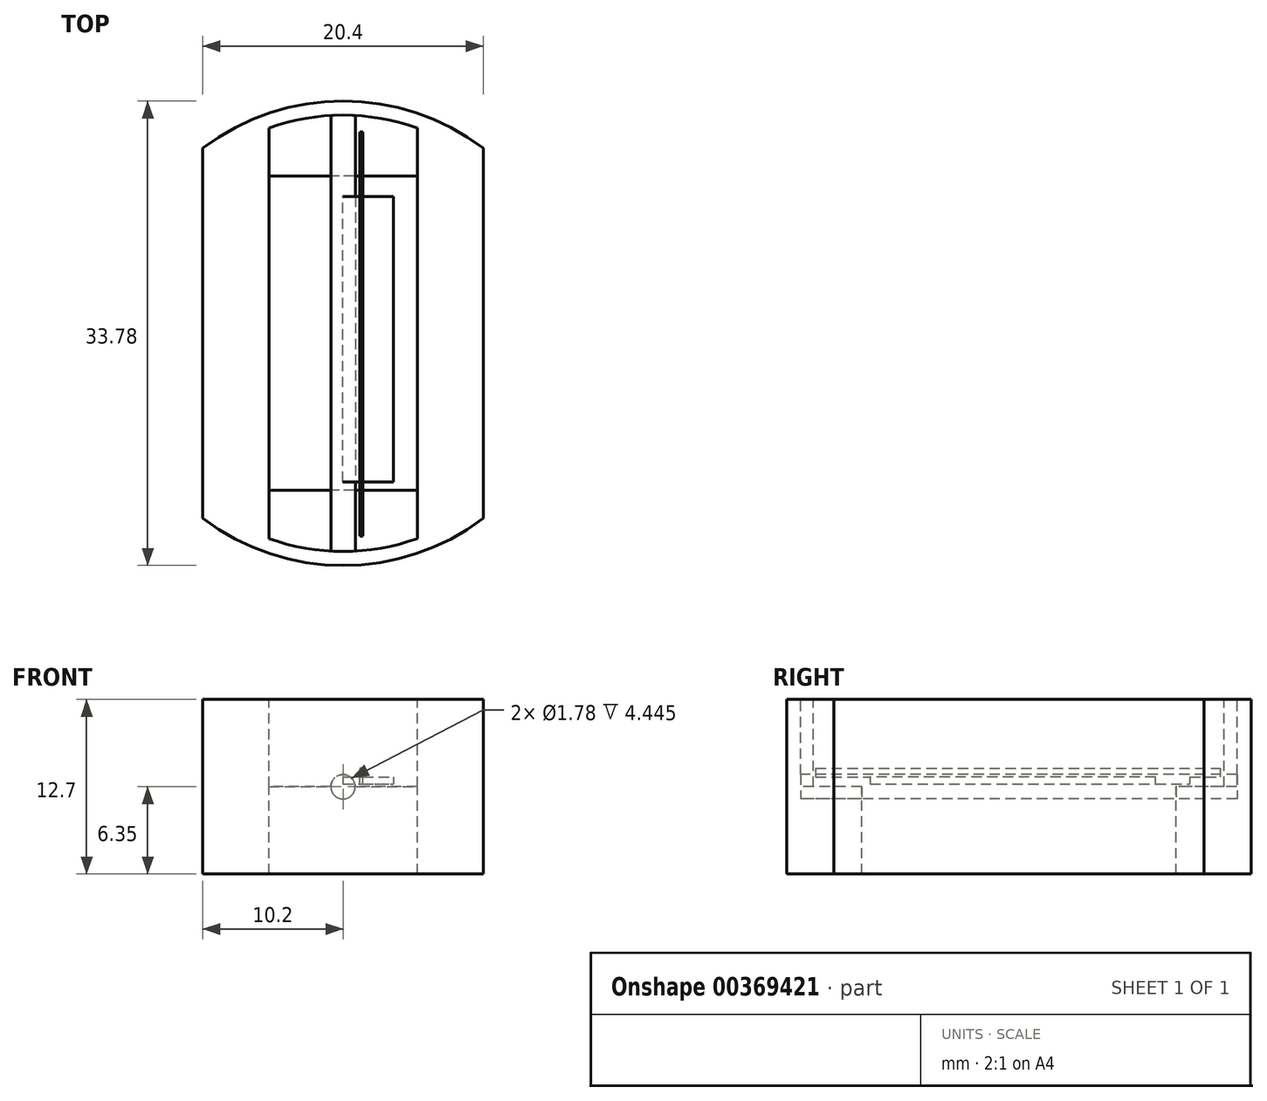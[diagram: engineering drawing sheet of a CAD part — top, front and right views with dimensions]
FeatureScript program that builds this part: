
annotation { "Feature Type Name" : "Feature", "Feature Type Description" : "" }
export const myFeature = defineFeature(function(context is Context, id is Id, definition is map)
    precondition{}
    {
        {
            var Q0;
            Q0=qCreatedBy(makeId("Top.planeOp"),FACE);
            var sketch = newSketch(context, id + "F0", { "sketchPlane" : qUnion([Q0])});
            skCircle(sketch, "E0", {"center": v(0, 0) * mm, "radius": 16.9 * mm});
            skSolve(sketch);
        }
        {
            var Q0;
            Q0 = qSketchRegion(id + "F0", true);
            var Q1;
            Q1 = qSketchRegion(id + "FndjnpffMJqqSbx_1", true);
            extrude(context, id + "F1", {"entities" : qUnion([Q0, Q1]), "depth" : 12.7 * mm});
        }
        {
            var Q0;
            Q0=qCreatedBy(makeId("Top.planeOp"),FACE);
            var sketch = newSketch(context, id + "F2", { "sketchPlane" : qUnion([Q0])});
            skLineSegment(sketch, "E1.bottom", {"start": v(-10.2, -16.71) * mm, "end": v(-23.15, -16.71) * mm});
            skLineSegment(sketch, "E1.top", {"start": v(-10.2, 16.78) * mm, "end": v(-23.15, 16.78) * mm});
            skLineSegment(sketch, "E1.left", {"start": v(-10.2, -16.71) * mm, "end": v(-10.2, 16.78) * mm});
            skLineSegment(sketch, "E1.right", {"start": v(-23.15, -16.71) * mm, "end": v(-23.15, 16.78) * mm});
            skSolve(sketch);
        }
        {
            var Q0;
            Q0=qCreatedBy(makeId("Top.planeOp"),FACE);
            var sketch = newSketch(context, id + "F3", { "sketchPlane" : qUnion([Q0])});
            skLineSegment(sketch, "E2.bottom", {"start": v(10.2, -16.64) * mm, "end": v(26.8, -16.64) * mm});
            skLineSegment(sketch, "E2.top", {"start": v(10.2, 17) * mm, "end": v(26.8, 17) * mm});
            skLineSegment(sketch, "E2.left", {"start": v(10.2, -16.64) * mm, "end": v(10.2, 17) * mm});
            skLineSegment(sketch, "E2.right", {"start": v(26.8, -16.64) * mm, "end": v(26.8, 17) * mm});
            skSolve(sketch);
        }
        {
            var Q0;
            Q0=makeQuery(id+"F2.imprint","IMPRINT",FACE,{"disambiguationData":[TD([[makeQuery(id+"F2.imprint","IMPRINT",EDGE,{"derivedFrom":sQuery(id+"F2.wireOp",EDGE,"E1.bottom")}),-1.0]])]});
            var Q1;
            Q1=makeQuery(id+"F3.imprint","IMPRINT",FACE,{"disambiguationData":[TD([[makeQuery(id+"F3.imprint","IMPRINT",EDGE,{"derivedFrom":sQuery(id+"F3.wireOp",EDGE,"E2.bottom")}),1.0]])]});
            extrude(context, id + "F4", {"entities" : qUnion([Q0, Q1]), "depth" : 12.7 * mm});
        }
        {
            var Q0;
            Q0=makeQuery(id+"F4.opExtrude","SWEPT_BODY",BODY,{"disambiguationData":[OSD([sQuery(id+"F2.wireOp",EDGE,"E1.bottom"),sQuery(id+"F2.wireOp",EDGE,"E1.top"),sQuery(id+"F2.wireOp",EDGE,"E1.left"),sQuery(id+"F2.wireOp",EDGE,"E1.right")])]});
            var Q1;
            Q1=makeQuery(id+"F4.opExtrude","SWEPT_BODY",BODY,{"disambiguationData":[OSD([sQuery(id+"F3.wireOp",EDGE,"E2.bottom"),sQuery(id+"F3.wireOp",EDGE,"E2.top"),sQuery(id+"F3.wireOp",EDGE,"E2.left"),sQuery(id+"F3.wireOp",EDGE,"E2.right")])]});
            var Q2;
            Q2=makeQuery(id+"F1.opExtrude","SWEPT_BODY",BODY,{"disambiguationData":[OSD([sQuery(id+"F0.wireOp",EDGE,"E0")])]});
            booleanBodies(context, id + "F5", {"operationType" : BooleanOperationType.SUBTRACTION, "tools" : qUnion([Q0, Q1]), "targets" : qUnion([Q2])});
        }
        {
            var Q0;
            Q0=qCreatedBy(makeId("Top.planeOp"),FACE);
            var sketch = newSketch(context, id + "F6", { "sketchPlane" : qUnion([Q0])});
            skLineSegment(sketch, "E3.bottom", {"start": v(5.4, -15.88) * mm, "end": v(-5.4, -15.88) * mm});
            skLineSegment(sketch, "E3.top", {"start": v(5.4, 15.88) * mm, "end": v(-5.4, 15.88) * mm});
            skLineSegment(sketch, "E3.left", {"start": v(5.4, -15.88) * mm, "end": v(5.4, 15.88) * mm});
            skLineSegment(sketch, "E3.right", {"start": v(-5.4, -15.88) * mm, "end": v(-5.4, 15.88) * mm});
            skPoint(sketch, "E3.middle", {"position": v(0, 0) * mm});
            skCircle(sketch, "E4", {"center": v(0, 0) * mm, "radius": 15.88 * mm});
            skSolve(sketch);
        }
        {
            var Q0;
            {var subQ0=sQuery(id+"F6.wireOp",EDGE,"E4");var subQ5=sQuery(id+"F6.wireOp",EDGE,"E3.left");var subQ7=makeQuery(id+"F6.imprint","INTERSECT",VERTEX,{"disambiguationData":[OD(0.0)],"derivedFrom":[subQ5,subQ0]});Q0=makeQuery(id+"F6.imprint","IMPRINT",FACE,{"disambiguationData":[TD([[makeQuery(id+"F6.imprint","IMPRINT",EDGE,{"disambiguationData":[TD([[subQ7,-1.0]])],"derivedFrom":subQ5}),1.0]])]});}
            extrude(context, id + "F7", {"entities" : qUnion([Q0]), "depth" : 6.35 * mm});
        }
        {
            var Q0;
            Q0=makeQuery(id+"F7.opExtrude","SWEPT_BODY",BODY,{"disambiguationData":[OSD([sQuery(id+"F6.wireOp",EDGE,"E3.left"),sQuery(id+"F6.wireOp",EDGE,"E3.right"),sQuery(id+"F6.wireOp",EDGE,"E4")])]});
            var Q1;
            Q1=makeQuery(id+"F1.opExtrude","SWEPT_BODY",BODY,{"disambiguationData":[OSD([sQuery(id+"F0.wireOp",EDGE,"E0")])]});
            booleanBodies(context, id + "F8", {"operationType" : BooleanOperationType.SUBTRACTION, "tools" : qUnion([Q0]), "targets" : qUnion([Q1])});
        }
        {
            var Q0;
            Q0=qCreatedBy(makeId("Top.planeOp"),FACE);
            var sketch = newSketch(context, id + "F9", { "sketchPlane" : qUnion([Q0])});
            skLineSegment(sketch, "E5.bottom", {"start": v(5.4, -11.43) * mm, "end": v(-5.4, -11.43) * mm});
            skLineSegment(sketch, "E5.top", {"start": v(5.4, 11.43) * mm, "end": v(-5.4, 11.43) * mm});
            skLineSegment(sketch, "E5.left", {"start": v(5.4, -11.43) * mm, "end": v(5.4, 11.43) * mm});
            skLineSegment(sketch, "E5.right", {"start": v(-5.4, -11.43) * mm, "end": v(-5.4, 11.43) * mm});
            skPoint(sketch, "E5.middle", {"position": v(0, 0) * mm});
            skSolve(sketch);
        }
        {
            var Q0;
            Q0 = qSketchRegion(id + "F9", true);
            extrude(context, id + "F10", {"entities" : qUnion([Q0]), "depth" : 12.7 * mm});
        }
        {
            var Q0;
            Q0=makeQuery(id+"F10.opExtrude","SWEPT_BODY",BODY,{"disambiguationData":[OSD([sQuery(id+"F9.wireOp",EDGE,"E5.bottom"),sQuery(id+"F9.wireOp",EDGE,"E5.top"),sQuery(id+"F9.wireOp",EDGE,"E5.left"),sQuery(id+"F9.wireOp",EDGE,"E5.right")])]});
            var Q1;
            Q1=makeQuery(id+"F1.opExtrude","SWEPT_BODY",BODY,{"disambiguationData":[OSD([sQuery(id+"F0.wireOp",EDGE,"E0")])]});
            booleanBodies(context, id + "F11", {"operationType" : BooleanOperationType.SUBTRACTION, "tools" : qUnion([Q0]), "targets" : qUnion([Q1])});
        }
        {
            var Q0;
            Q0=qCreatedBy(makeId("Front.planeOp"),FACE);
            var sketch = newSketch(context, id + "F12", { "sketchPlane" : qUnion([Q0])});
            skCircle(sketch, "E6", {"center": v(0, 0) * mm, "radius": 0.89 * mm});
            skSolve(sketch);
        }
        {
            var Q0;
            Q0=makeQuery(id+"F12.imprint","IMPRINT",FACE,{"disambiguationData":[TD([[makeQuery(id+"F12.imprint","IMPRINT",EDGE,{"derivedFrom":sQuery(id+"F12.wireOp",EDGE,"E6")}),1.0]])]});
            extrude(context, id + "F13", {"entities" : qUnion([Q0]), "depth" : 31.75 * mm});
        }
        {
            var Q0;
            Q0=makeQuery(id+"F13.opExtrude","SWEPT_BODY",BODY,{"disambiguationData":[OSD([sQuery(id+"F12.wireOp",EDGE,"E6")])]});
            transform(context, id + "F14", {"entities" : qUnion([Q0]), "transformType" : TransformType.TRANSLATION_3D, "dx" : 0 * mm, "dy" : 15.88 * mm, "dz" : 6.35 * mm, "makeCopy" : false});
        }
        {
            var Q0;
            Q0=makeQuery(id+"F13.opExtrude","SWEPT_BODY",BODY,{"disambiguationData":[OSD([sQuery(id+"F12.wireOp",EDGE,"E6")])]});
            var Q1;
            Q1=makeQuery(id+"F1.opExtrude","SWEPT_BODY",BODY,{"disambiguationData":[OSD([sQuery(id+"F0.wireOp",EDGE,"E0")])]});
            booleanBodies(context, id + "F15", {"operationType" : BooleanOperationType.SUBTRACTION, "tools" : qUnion([Q0]), "targets" : qUnion([Q1]), "keepTools" : true});
        }
        {
            var Q0;
            Q0=qCreatedBy(makeId("Top.planeOp"),FACE);
            var sketch = newSketch(context, id + "F16", { "sketchPlane" : qUnion([Q0])});
            skLineSegment(sketch, "E7", {"start": v(-67.14, 0) * mm, "end": v(70.94, 0) * mm});
            skSolve(sketch);
        }
        {
            var Q0;
            Q0=makeQuery(id+"F1.opExtrude","SWEPT_BODY",BODY,{"disambiguationData":[OSD([sQuery(id+"F0.wireOp",EDGE,"E0")])]});
            var Q1;
            Q1=makeQuery(id+"F13.opExtrude","SWEPT_BODY",BODY,{"disambiguationData":[OSD([sQuery(id+"F12.wireOp",EDGE,"E6")])]});
            var Q2;
            Q2=sQuery(id+"F16.wireOp",EDGE,"E7");
            transform(context, id + "F17", {"entities" : qUnion([Q0, Q1]), "transformType" : TransformType.ROTATION, "transformAxis" : qUnion([Q2]), "angle" : 180 * degree, "makeCopy" : false});
        }
        {
            var Q0;
            Q0=qCreatedBy(makeId("Top.planeOp"),FACE);
            var sketch = newSketch(context, id + "F18", { "sketchPlane" : qUnion([Q0])});
            skLineSegment(sketch, "E8.bottom", {"start": v(-0.01, -10.8) * mm, "end": v(3.66, -10.8) * mm});
            skLineSegment(sketch, "E8.top", {"start": v(-0.01, 9.95) * mm, "end": v(3.66, 9.95) * mm});
            skLineSegment(sketch, "E8.left", {"start": v(-0.01, -10.8) * mm, "end": v(-0.01, 9.95) * mm});
            skLineSegment(sketch, "E8.right", {"start": v(3.66, -10.8) * mm, "end": v(3.66, 9.95) * mm});
            skSolve(sketch);
        }
        {
            var Q0;
            Q0=makeQuery(id+"F18.imprint","IMPRINT",FACE,{"disambiguationData":[TD([[makeQuery(id+"F18.imprint","IMPRINT",EDGE,{"derivedFrom":sQuery(id+"F18.wireOp",EDGE,"E8.bottom")}),1.0]])]});
            extrude(context, id + "F19", {"entities" : qUnion([Q0]), "depth" : 0.5 * mm});
        }
        {
            var Q0;
            Q0=makeQuery(id+"F19.opExtrude","SWEPT_BODY",BODY,{"disambiguationData":[OSD([sQuery(id+"F18.wireOp",EDGE,"E8.bottom"),sQuery(id+"F18.wireOp",EDGE,"E8.top"),sQuery(id+"F18.wireOp",EDGE,"E8.left"),sQuery(id+"F18.wireOp",EDGE,"E8.right")])]});
            transform(context, id + "F20", {"entities" : qUnion([Q0]), "transformType" : TransformType.TRANSLATION_3D, "dx" : 0 * mm, "dy" : 0 * mm, "dz" : -6.15 * mm, "makeCopy" : false});
        }
        {
            var Q0;
            Q0=makeQuery(id+"F19.opExtrude","CAP_FACE",FACE,{"disambiguationData":[OSD([sQuery(id+"F18.wireOp",EDGE,"E8.bottom"),sQuery(id+"F18.wireOp",EDGE,"E8.top"),sQuery(id+"F18.wireOp",EDGE,"E8.left"),sQuery(id+"F18.wireOp",EDGE,"E8.right")])],"isStart":false});
            var sketch = newSketch(context, id + "F21", { "sketchPlane" : qUnion([Q0])});
            skLineSegment(sketch, "E9.bottom", {"start": v(1.45, -14.77) * mm, "end": v(1.22, -14.77) * mm});
            skLineSegment(sketch, "E9.top", {"start": v(1.45, 14.65) * mm, "end": v(1.22, 14.65) * mm});
            skLineSegment(sketch, "E9.left", {"start": v(1.45, -14.77) * mm, "end": v(1.45, 14.65) * mm});
            skLineSegment(sketch, "E9.right", {"start": v(1.22, -14.77) * mm, "end": v(1.22, 14.65) * mm});
            skSolve(sketch);
        }
        {
            var Q0;
            {var subQ0=sQuery(id+"F21.wireOp",EDGE,"E9.top");Q0=makeQuery(id+"F21.imprint","IMPRINT",FACE,{"disambiguationData":[TD([[makeQuery(id+"F21.imprint","IMPRINT",EDGE,{"derivedFrom":subQ0}),1.0]])]});}
            var Q1;
            {var subQ0=sQuery(id+"F21.wireOp",EDGE,"E9.left");var subQ1=makeQuery(id+"F19.opExtrude","CAP_EDGE",EDGE,{"disambiguationData":[OSD([sQuery(id+"F18.wireOp",EDGE,"E8.bottom")])],"isStart":false});var subQ2=makeQuery(id+"F21.imprint","INTERSECT",VERTEX,{"derivedFrom":[subQ1,subQ0]});Q1=makeQuery(id+"F21.imprint","IMPRINT",FACE,{"disambiguationData":[TD([[makeQuery(id+"F21.imprint","IMPRINT",EDGE,{"disambiguationData":[TD([[subQ2,-1.0]])],"derivedFrom":subQ0}),1.0]])]});}
            var Q2;
            {var subQ0=sQuery(id+"F21.wireOp",EDGE,"E9.bottom");Q2=makeQuery(id+"F21.imprint","IMPRINT",FACE,{"disambiguationData":[TD([[makeQuery(id+"F21.imprint","IMPRINT",EDGE,{"derivedFrom":subQ0}),-1.0]])]});}
            extrude(context, id + "F22", {"entities" : qUnion([Q0, Q1, Q2]), "depth" : 0.64 * mm});
        }
        {
            var Q0;
            Q0=makeQuery(id+"F22.opExtrude","CAP_FACE",FACE,{"disambiguationData":[OSD([sQuery(id+"F21.wireOp",EDGE,"E9.bottom"),sQuery(id+"F21.wireOp",EDGE,"E9.top"),sQuery(id+"F21.wireOp",EDGE,"E9.left"),sQuery(id+"F21.wireOp",EDGE,"E9.right")])],"isStart":true});
            var sketch = newSketch(context, id + "F23", { "sketchPlane" : qUnion([Q0])});
            skLineSegment(sketch, "E10.bottom", {"start": v(1.22, -7.22) * mm, "end": v(1.45, -7.22) * mm});
            skLineSegment(sketch, "E10.top", {"start": v(1.22, -12.46) * mm, "end": v(1.45, -12.46) * mm});
            skLineSegment(sketch, "E10.left", {"start": v(1.22, -7.22) * mm, "end": v(1.22, -12.46) * mm});
            skLineSegment(sketch, "E10.right", {"start": v(1.45, -7.22) * mm, "end": v(1.45, -12.46) * mm});
            skSolve(sketch);
        }
        {
            var Q0;
            Q0=makeQuery(id+"F23.imprint","IMPRINT",FACE,{"disambiguationData":[TD([[makeQuery(id+"F23.imprint","IMPRINT",EDGE,{"derivedFrom":sQuery(id+"F23.wireOp",EDGE,"E10.bottom")}),-1.0]])]});
            extrude(context, id + "F24", {"entities" : qUnion([Q0]), "operationType" : NewBodyOperationType.ADD, "depth" : 0.5 * mm});
        }
    });
